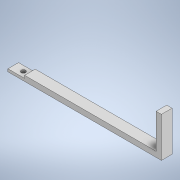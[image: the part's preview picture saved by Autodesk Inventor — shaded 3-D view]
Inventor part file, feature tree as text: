
AUTODESK INVENTOR PART (.ipt)
format: ipt  version: 2020.2 (Build 242310000, 310)  size: 134,144 bytes
history: native  units: mm
features: sketch x4, extrude x4, hole x1, projected_geometry x1
ambient origin geometry x8: Origin, YZ Plane, XZ Plane, XY Plane, X Axis, Y Axis, Z Axis, Center Point
bodies: Solid1 (feature_tree)
feature tree (10):
  sketch  "Sketch1"  dims[d0=98.806mm d1=8.0mm]
  extrude  "Extrusion1"  Depth=8.0mm
  extrude  "Extrusion2"  Depth=8.0mm
  hole  "Hole1"  [1 undecoded]
  extrude  "Extrusion3"  Depth=10.0mm
  extrude  "Extrusion4"  Depth=8.0mm
  sketch  "Sketch2"  dims[d2=4.0mm d3=8.0mm]
  sketch  "Sketch3"  dims[d4=10.0mm d5=30.0mm d6=0.0mm]
  sketch  "Sketch4"  dims[d7=4.0mm d8=0.0mm d9=5.0mm d10=3.4mm d11=6.0mm d12=6.3mm d13=2.0mm d14=90.0deg d15=8.0mm d16=20.594885mm d17=8.0mm d18=2.0mm d19=10.0mm d20=0.0mm d21=2.54mm d22=0.0mm]
  projected_geometry  "Projected Loop1"
note: 1 required parameter value undecoded (feature->parameter linkage not recoverable at this tier; creation-order binding heuristic only, values carry confidence <= 0.55)
